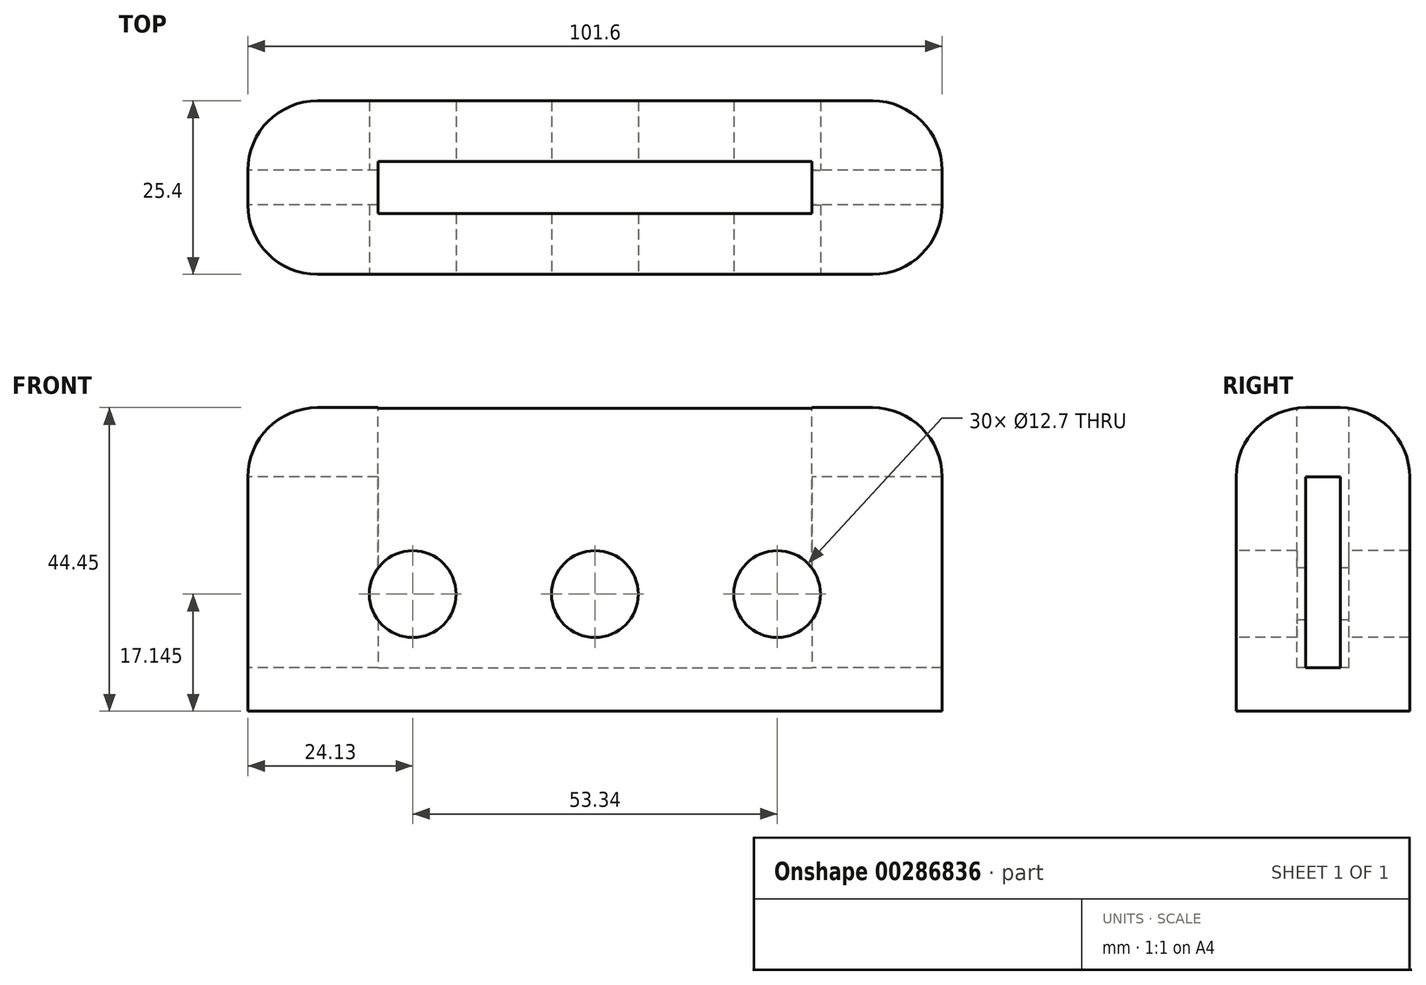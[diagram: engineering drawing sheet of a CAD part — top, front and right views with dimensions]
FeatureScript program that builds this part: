
annotation { "Feature Type Name" : "Feature", "Feature Type Description" : "" }
export const myFeature = defineFeature(function(context is Context, id is Id, definition is map)
    precondition{}
    {
        {
            var Q0;
            Q0=qCreatedBy(makeId("Front.planeOp"),FACE);
            var sketch = newSketch(context, id + "F0", { "sketchPlane" : qUnion([Q0])});
            skLineSegment(sketch, "E0.bottom", {"start": v(-101.6, 0) * mm, "end": v(0, 0) * mm});
            skLineSegment(sketch, "E0.top", {"start": v(-101.6, -44.45) * mm, "end": v(0, -44.45) * mm});
            skLineSegment(sketch, "E0.left", {"start": v(-101.6, 0) * mm, "end": v(-101.6, -44.45) * mm});
            skLineSegment(sketch, "E0.right", {"start": v(0, 0) * mm, "end": v(0, -44.45) * mm});
            skSolve(sketch);
        }
        {
            var Q0;
            Q0=makeQuery(id+"F0.imprint","IMPRINT",FACE,{"disambiguationData":[TD([[makeQuery(id+"F0.imprint","IMPRINT",EDGE,{"derivedFrom":sQuery(id+"F0.wireOp",EDGE,"E0.bottom")}),-1.0]])]});
            extrude(context, id + "F1", {"entities" : qUnion([Q0]), "depth" : 25.4 * mm});
        }
        {
            var Q0;
            Q0=makeQuery(id+"F1.opExtrude","CAP_EDGE",EDGE,{"disambiguationData":[OSD([sQuery(id+"F0.wireOp",EDGE,"E0.bottom")])],"isStart":false});
            var Q1;
            Q1=makeQuery(id+"F1.opExtrude","SWEPT_EDGE",EDGE,{"disambiguationData":[OSD([sQuery(id+"F0.wireOp",EDGE,"E0.bottom"),sQuery(id+"F0.wireOp",EDGE,"E0.right")])]});
            var Q2;
            Q2=makeQuery(id+"F1.opExtrude","CAP_EDGE",EDGE,{"disambiguationData":[OSD([sQuery(id+"F0.wireOp",EDGE,"E0.right")])],"isStart":false});
            var Q3;
            Q3=makeQuery(id+"F1.opExtrude","CAP_EDGE",EDGE,{"disambiguationData":[OSD([sQuery(id+"F0.wireOp",EDGE,"E0.right")])],"isStart":true});
            var Q4;
            Q4=makeQuery(id+"F1.opExtrude","CAP_EDGE",EDGE,{"disambiguationData":[OSD([sQuery(id+"F0.wireOp",EDGE,"E0.left")])],"isStart":false});
            var Q5;
            Q5=makeQuery(id+"F1.opExtrude","SWEPT_EDGE",EDGE,{"disambiguationData":[OSD([sQuery(id+"F0.wireOp",EDGE,"E0.bottom"),sQuery(id+"F0.wireOp",EDGE,"E0.left")])]});
            var Q6;
            Q6=makeQuery(id+"F1.opExtrude","CAP_EDGE",EDGE,{"disambiguationData":[OSD([sQuery(id+"F0.wireOp",EDGE,"E0.bottom")])],"isStart":true});
            var Q7;
            Q7=makeQuery(id+"F1.opExtrude","CAP_EDGE",EDGE,{"disambiguationData":[OSD([sQuery(id+"F0.wireOp",EDGE,"E0.left")])],"isStart":true});
            fillet(context, id + "F2", {"entities" : qUnion([Q0, Q1, Q2, Q3, Q4, Q5, Q6, Q7]), "radius" : 10.16 * mm, "tangentPropagation" : true, "allowEdgeOverflow" : false});
        }
        {
            var Q0;
            Q0=makeQuery(id+"F1.opExtrude","SWEPT_FACE",FACE,{"disambiguationData":[OSD([sQuery(id+"F0.wireOp",EDGE,"E0.left")])]});
            var sketch = newSketch(context, id + "F3", { "sketchPlane" : qUnion([Q0])});
            skLineSegment(sketch, "E1.bottom", {"start": v(10.16, -10.16) * mm, "end": v(15.24, -10.16) * mm});
            skLineSegment(sketch, "E1.top", {"start": v(10.16, -38.1) * mm, "end": v(15.24, -38.1) * mm});
            skLineSegment(sketch, "E1.left", {"start": v(10.16, -10.16) * mm, "end": v(10.16, -38.1) * mm});
            skLineSegment(sketch, "E1.right", {"start": v(15.24, -10.16) * mm, "end": v(15.24, -38.1) * mm});
            skLineSegment(sketch, "E2", {"start": v(12.7, -44.45) * mm, "end": v(12.7, -38.1) * mm});
            skSolve(sketch);
        }
        {
            var Q0;
            Q0 = qSketchRegion(id + "F3", true);
            extrude(context, id + "F4", {"entities" : qUnion([Q0]), "operationType" : NewBodyOperationType.REMOVE, "oppositeDirection" : true, "depth" : 101.6 * mm});
        }
        {
            var Q0;
            Q0=makeQuery(id+"F1.opExtrude","CAP_FACE",FACE,{"disambiguationData":[OSD([sQuery(id+"F0.wireOp",EDGE,"E0.bottom"),sQuery(id+"F0.wireOp",EDGE,"E0.top"),sQuery(id+"F0.wireOp",EDGE,"E0.left"),sQuery(id+"F0.wireOp",EDGE,"E0.right")])],"isStart":false});
            var sketch = newSketch(context, id + "F5", { "sketchPlane" : qUnion([Q0])});
            skCircle(sketch, "E3", {"center": v(-77.47, -27.3) * mm, "radius": 6.35 * mm});
            skCircle(sketch, "E4", {"center": v(-50.8, -27.3) * mm, "radius": 6.35 * mm});
            skCircle(sketch, "E5", {"center": v(-24.13, -27.3) * mm, "radius": 6.35 * mm});
            skLineSegment(sketch, "E6", {"start": v(-50.8, -27.3) * mm, "end": v(-91.44, -27.3) * mm});
            skLineSegment(sketch, "E7", {"start": v(-50.8, -27.3) * mm, "end": v(-10.16, -27.3) * mm});
            skLineSegment(sketch, "E8", {"start": v(-57.15, -27.3) * mm, "end": v(-71.12, -27.3) * mm});
            skLineSegment(sketch, "E9", {"start": v(-91.44, -27.3) * mm, "end": v(-77.47, -27.3) * mm});
            skLineSegment(sketch, "E10", {"start": v(-24.13, -27.3) * mm, "end": v(-10.16, -27.3) * mm});
            skLineSegment(sketch, "E11", {"start": v(-44.45, -27.3) * mm, "end": v(-30.48, -27.3) * mm});
            skLineSegment(sketch, "E12", {"start": v(-77.47, -27.3) * mm, "end": v(-77.47, -10.16) * mm});
            skLineSegment(sketch, "E13", {"start": v(-77.47, -27.3) * mm, "end": v(-77.47, -44.45) * mm});
            skSolve(sketch);
        }
        {
            var Q0;
            Q0 = qSketchRegion(id + "F5", true);
            extrude(context, id + "F6", {"entities" : qUnion([Q0]), "operationType" : NewBodyOperationType.REMOVE, "oppositeDirection" : true, "depth" : 25.4 * mm});
        }
        {
            var Q0;
            Q0=makeQuery(id+"F1.opExtrude","SWEPT_FACE",FACE,{"disambiguationData":[OSD([sQuery(id+"F0.wireOp",EDGE,"E0.bottom")])]});
            var sketch = newSketch(context, id + "F7", { "sketchPlane" : qUnion([Q0])});
            skLineSegment(sketch, "E14.bottom", {"start": v(-82.55, -8.9) * mm, "end": v(-19.05, -8.9) * mm});
            skLineSegment(sketch, "E14.top", {"start": v(-82.55, -16.51) * mm, "end": v(-19.05, -16.51) * mm});
            skLineSegment(sketch, "E14.left", {"start": v(-82.55, -8.89) * mm, "end": v(-82.55, -16.51) * mm});
            skLineSegment(sketch, "E14.right", {"start": v(-19.05, -8.89) * mm, "end": v(-19.05, -16.51) * mm});
            skLineSegment(sketch, "E15", {"start": v(-91.44, -12.7) * mm, "end": v(-82.55, -12.7) * mm});
            skLineSegment(sketch, "E16", {"start": v(-19.05, -12.7) * mm, "end": v(-10.16, -12.7) * mm});
            skLineSegment(sketch, "E17", {"start": v(-50.8, -8.9) * mm, "end": v(-50.8, -10.16) * mm});
            skLineSegment(sketch, "E18", {"start": v(-50.8, -15.24) * mm, "end": v(-50.8, -16.51) * mm});
            skSolve(sketch);
        }
        {
            var Q0;
            Q0 = qSketchRegion(id + "F7", true);
            extrude(context, id + "F8", {"entities" : qUnion([Q0]), "operationType" : NewBodyOperationType.REMOVE, "oppositeDirection" : true, "depth" : 38.1 * mm});
        }
    });
